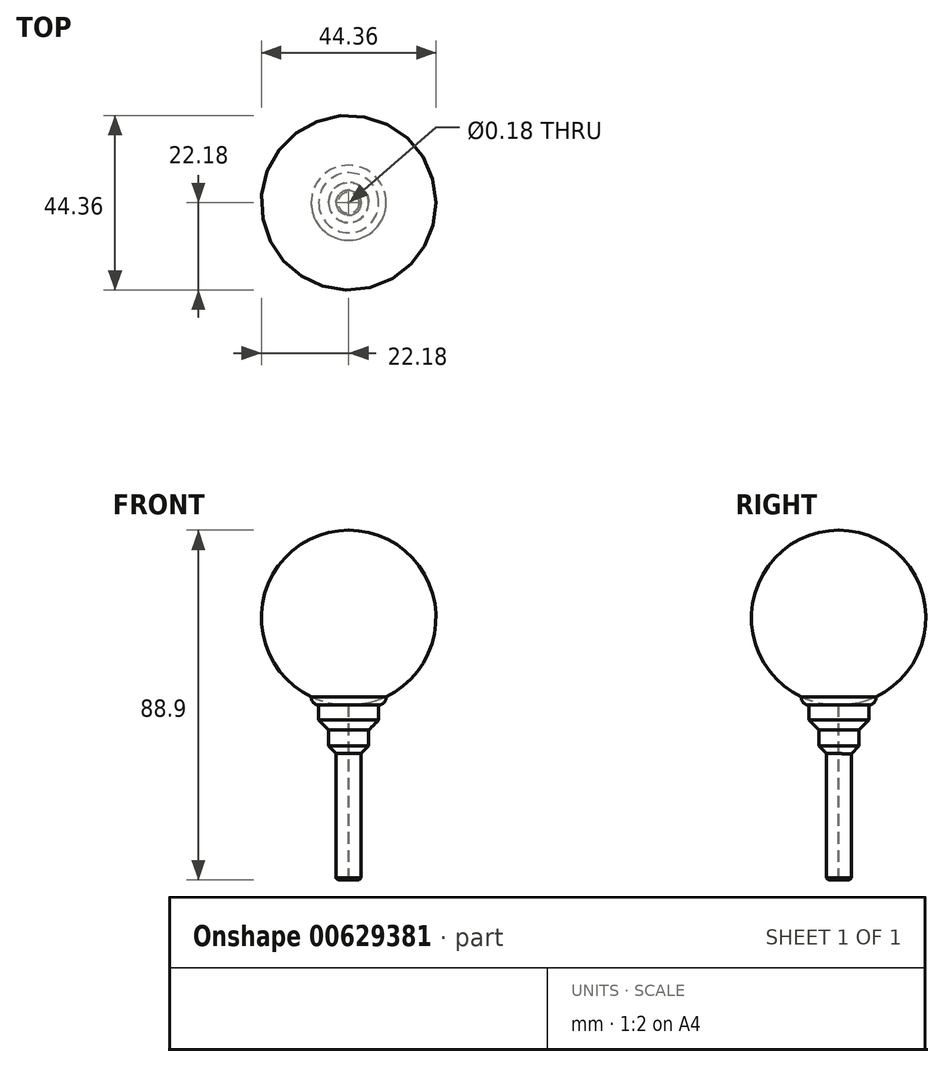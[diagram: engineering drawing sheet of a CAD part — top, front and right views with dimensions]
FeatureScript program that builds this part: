
annotation { "Feature Type Name" : "Feature", "Feature Type Description" : "" }
export const myFeature = defineFeature(function(context is Context, id is Id, definition is map)
    precondition{}
    {
        {
            var Q0;
            Q0=qCreatedBy(makeId("Front.planeOp"),FACE);
            var sketch = newSketch(context, id + "F0", { "sketchPlane" : qUnion([Q0])});
            skLineSegment(sketch, "E0", {"start": v(0, 0) * mm, "end": v(0, 44.45) * mm});
            skArc(sketch, "E1", {"start": v(0, 44.45) * mm, "mid": v(-22.27, 22.23) * mm, "end": v(0, 0) * mm});
            skSolve(sketch);
        }
        {
            var Q0;
            Q0=makeQuery(id+"F0.imprint","IMPRINT",FACE,{"disambiguationData":[TD([[makeQuery(id+"F0.imprint","IMPRINT",EDGE,{"derivedFrom":sQuery(id+"F0.wireOp",EDGE,"E0")}),1.0]])]});
            var Q1;
            Q1=sQuery(id+"F0.wireOp",EDGE,"E0");
            revolve(context, id + "F1", {"entities" : qUnion([Q0]), "axis" : qUnion([Q1]), "revolveType" : RevolveType.FULL});
        }
        {
            var Q0;
            Q0=qCreatedBy(makeId("Top.planeOp"),FACE);
            var sketch = newSketch(context, id + "F2", { "sketchPlane" : qUnion([Q0])});
            skCircle(sketch, "E2", {"center": v(0, 0) * mm, "radius": 9.53 * mm});
            skSolve(sketch);
        }
        {
            var Q0;
            Q0=makeQuery(id+"F2.imprint","IMPRINT",FACE,{"disambiguationData":[TD([[makeQuery(id+"F2.imprint","IMPRINT",EDGE,{"derivedFrom":sQuery(id+"F2.wireOp",EDGE,"E2")}),1.0]])]});
            extrude(context, id + "F3", {"entities" : qUnion([Q0]), "operationType" : NewBodyOperationType.ADD, "depth" : 19.05 * mm, "offsetDistance" : 25.4 * mm});
        }
        {
            var Q0;
            Q0=makeQuery(id+"F3.opExtrude","CAP_FACE",FACE,{"disambiguationData":[OSD([sQuery(id+"F2.wireOp",EDGE,"E2")])],"isStart":true});
            var sketch = newSketch(context, id + "F4", { "sketchPlane" : qUnion([Q0])});
            skCircle(sketch, "E3", {"center": v(0, 0) * mm, "radius": 7.62 * mm});
            skSolve(sketch);
        }
        {
            var Q0;
            Q0=makeQuery(id+"F4.imprint","IMPRINT",FACE,{"disambiguationData":[TD([[makeQuery(id+"F4.imprint","IMPRINT",EDGE,{"derivedFrom":sQuery(id+"F4.wireOp",EDGE,"E3")}),1.0]])]});
            extrude(context, id + "F5", {"entities" : qUnion([Q0]), "operationType" : NewBodyOperationType.ADD, "depth" : 6.35 * mm, "offsetDistance" : 25.4 * mm});
        }
        {
            var Q0;
            Q0=makeQuery(id+"F5.opExtrude","CAP_FACE",FACE,{"disambiguationData":[OSD([sQuery(id+"F0.wireOp",EDGE,"E1"),sQuery(id+"F2.wireOp",EDGE,"E2"),sQuery(id+"F4.wireOp",EDGE,"E3")])],"isStart":false});
            var sketch = newSketch(context, id + "F6", { "sketchPlane" : qUnion([Q0])});
            skCircle(sketch, "E4", {"center": v(0, -0.1) * mm, "radius": 5.08 * mm});
            skSolve(sketch);
        }
        {
            var Q0;
            Q0=makeQuery(id+"F6.imprint","IMPRINT",FACE,{"disambiguationData":[TD([[makeQuery(id+"F6.imprint","IMPRINT",EDGE,{"derivedFrom":sQuery(id+"F6.wireOp",EDGE,"E4")}),1.0]])]});
            extrude(context, id + "F7", {"entities" : qUnion([Q0]), "operationType" : NewBodyOperationType.ADD, "depth" : 6.35 * mm, "offsetDistance" : 25.4 * mm});
        }
        {
            var Q0;
            Q0=makeQuery(id+"F7.opExtrude","CAP_FACE",FACE,{"disambiguationData":[OSD([sQuery(id+"F0.wireOp",EDGE,"E1"),sQuery(id+"F2.wireOp",EDGE,"E2"),sQuery(id+"F6.wireOp",EDGE,"E4")])],"isStart":false});
            var sketch = newSketch(context, id + "F8", { "sketchPlane" : qUnion([Q0])});
            skCircle(sketch, "E5", {"center": v(0, 0) * mm, "radius": 3.18 * mm});
            skSolve(sketch);
        }
        {
            var Q0;
            Q0=makeQuery(id+"F8.imprint","IMPRINT",FACE,{"disambiguationData":[TD([[makeQuery(id+"F8.imprint","IMPRINT",EDGE,{"derivedFrom":sQuery(id+"F8.wireOp",EDGE,"E5")}),1.0]])]});
            extrude(context, id + "F9", {"entities" : qUnion([Q0]), "operationType" : NewBodyOperationType.ADD, "depth" : 31.75 * mm, "offsetDistance" : 25.4 * mm});
        }
        {
            var Q0;
            Q0=makeQuery(id+"F3.opExtrude","CAP_EDGE",EDGE,{"disambiguationData":[OSD([sQuery(id+"F2.wireOp",EDGE,"E2")])],"isStart":true});
            fillet(context, id + "F10", {"entities" : qUnion([Q0]), "radius" : 2.03 * mm, "tangentPropagation" : true, "allowEdgeOverflow" : false});
        }
        {
            var Q0;
            Q0=makeQuery(id+"F5.opExtrude","CAP_EDGE",EDGE,{"disambiguationData":[OSD([sQuery(id+"F4.wireOp",EDGE,"E3")])],"isStart":false});
            chamfer(context, id + "F11", {"entities" : qUnion([Q0]), "width" : 2.54 * mm, "tangentPropagation" : true});
        }
        {
            var Q0;
            Q0=makeQuery(id+"F7.opExtrude","CAP_EDGE",EDGE,{"disambiguationData":[OSD([sQuery(id+"F6.wireOp",EDGE,"E4")])],"isStart":false});
            chamfer(context, id + "F12", {"entities" : qUnion([Q0]), "width" : 2.3 * mm, "tangentPropagation" : true});
        }
        {
            var Q0;
            Q0=makeQuery(id+"F9.opExtrude","CAP_EDGE",EDGE,{"disambiguationData":[OSD([sQuery(id+"F8.wireOp",EDGE,"E5")])],"isStart":false});
            chamfer(context, id + "F13", {"entities" : qUnion([Q0]), "width" : 0.5 * mm, "tangentPropagation" : true});
        }
        {
            var Q0;
            Q0=qCreatedBy(makeId("Front.planeOp"),FACE);
            cPlane(context, id + "F14", {"entities" : qUnion([Q0]), "cplaneType" : CPlaneType.OFFSET, "offset" : 25.9 * mm, "oppositeDirection" : true, "width" : 152.4 * mm, "height" : 152.4 * mm});
        }
        {
            var Q0;
            Q0=qCreatedBy(id+"F14.planeOp",FACE);
            var sketch = newSketch(context, id + "F15", { "sketchPlane" : qUnion([Q0])});
            skCircle(sketch, "E6", {"center": v(0, 22.74) * mm, "radius": 15.88 * mm});
            skSolve(sketch);
        }
        {
            var Q0;
            Q0=makeQuery(id+"F15.imprint","IMPRINT",FACE,{"disambiguationData":[TD([[makeQuery(id+"F15.imprint","IMPRINT",EDGE,{"derivedFrom":sQuery(id+"F15.wireOp",EDGE,"E6")}),1.0]])]});
            extrude(context, id + "F16", {"entities" : qUnion([Q0]), "operationType" : NewBodyOperationType.ADD, "depth" : 17.78 * mm, "offsetDistance" : 25.4 * mm});
        }
        {
            var Q0;
            Q0=makeQuery(id+"F16.opExtrude","CAP_FACE",FACE,{"disambiguationData":[OSD([sQuery(id+"F15.wireOp",EDGE,"E6")])],"isStart":true});
            var sketch = newSketch(context, id + "F17", { "sketchPlane" : qUnion([Q0])});
            skCircle(sketch, "E7", {"center": v(0, 22.74) * mm, "radius": 12.7 * mm});
            skSolve(sketch);
        }
        {
            var Q0;
            Q0=makeQuery(id+"F17.imprint","IMPRINT",FACE,{"disambiguationData":[TD([[makeQuery(id+"F17.imprint","IMPRINT",EDGE,{"derivedFrom":sQuery(id+"F17.wireOp",EDGE,"E7")}),1.0]])]});
            extrude(context, id + "F18", {"entities" : qUnion([Q0]), "operationType" : NewBodyOperationType.ADD, "depth" : 19.05 * mm, "offsetDistance" : 25.4 * mm});
        }
        {
            var Q0;
            Q0=makeQuery(id+"F18.opExtrude","CAP_FACE",FACE,{"disambiguationData":[OSD([sQuery(id+"F17.wireOp",EDGE,"E7")])],"isStart":false});
            var sketch = newSketch(context, id + "F19", { "sketchPlane" : qUnion([Q0])});
            skCircle(sketch, "E8", {"center": v(0, 22.74) * mm, "radius": 9.53 * mm});
            skSolve(sketch);
        }
        {
            var Q0;
            Q0=makeQuery(id+"F19.imprint","IMPRINT",FACE,{"disambiguationData":[TD([[makeQuery(id+"F19.imprint","IMPRINT",EDGE,{"derivedFrom":sQuery(id+"F19.wireOp",EDGE,"E8")}),1.0]])]});
            extrude(context, id + "F20", {"entities" : qUnion([Q0]), "operationType" : NewBodyOperationType.ADD, "depth" : 17.78 * mm, "offsetDistance" : 25.4 * mm});
        }
        {
            var Q0;
            Q0=makeQuery(id+"F20.opExtrude","CAP_FACE",FACE,{"disambiguationData":[OSD([sQuery(id+"F19.wireOp",EDGE,"E8")])],"isStart":false});
            var sketch = newSketch(context, id + "F21", { "sketchPlane" : qUnion([Q0])});
            skCircle(sketch, "E9", {"center": v(0, 22.74) * mm, "radius": 6.35 * mm});
            skSolve(sketch);
        }
        {
            var Q0;
            Q0=makeQuery(id+"F21.imprint","IMPRINT",FACE,{"disambiguationData":[TD([[makeQuery(id+"F21.imprint","IMPRINT",EDGE,{"derivedFrom":sQuery(id+"F21.wireOp",EDGE,"E9")}),1.0]])]});
            extrude(context, id + "F22", {"entities" : qUnion([Q0]), "operationType" : NewBodyOperationType.ADD, "depth" : 68.58 * mm, "offsetDistance" : 25.4 * mm});
        }
        {
            var Q0;
            Q0=makeQuery(id+"F16.opExtrude","CAP_EDGE",EDGE,{"disambiguationData":[OSD([sQuery(id+"F15.wireOp",EDGE,"E6")])],"isStart":true});
            fillet(context, id + "F23", {"entities" : qUnion([Q0]), "radius" : 15.87 * mm, "tangentPropagation" : true, "allowEdgeOverflow" : false});
        }
        {
            var Q0;
            Q0=makeQuery(id+"F18.opExtrude","CAP_EDGE",EDGE,{"disambiguationData":[OSD([sQuery(id+"F17.wireOp",EDGE,"E7")])],"isStart":false});
            chamfer(context, id + "F24", {"entities" : qUnion([Q0]), "width" : 6.35 * mm, "tangentPropagation" : true});
        }
        {
            var Q0;
            Q0=makeQuery(id+"F20.opExtrude","CAP_EDGE",EDGE,{"disambiguationData":[OSD([sQuery(id+"F19.wireOp",EDGE,"E8")])],"isStart":false});
            chamfer(context, id + "F25", {"entities" : qUnion([Q0]), "width" : 7.62 * mm, "tangentPropagation" : true});
        }
        {
            var Q0;
            Q0=makeQuery(id+"F22.opExtrude","CAP_EDGE",EDGE,{"disambiguationData":[OSD([sQuery(id+"F21.wireOp",EDGE,"E9")])],"isStart":false});
            chamfer(context, id + "F26", {"entities" : qUnion([Q0]), "width" : 1.02 * mm, "tangentPropagation" : true});
        }
        {
            var Q0;
            Q0=qCreatedBy(makeId("Right.planeOp"),FACE);
            cPlane(context, id + "F27", {"entities" : qUnion([Q0]), "cplaneType" : CPlaneType.OFFSET, "offset" : 24.64 * mm, "width" : 152.4 * mm, "height" : 152.4 * mm});
        }
        {
            var Q0;
            Q0=qCreatedBy(id+"F27.planeOp",FACE);
            var sketch = newSketch(context, id + "F28", { "sketchPlane" : qUnion([Q0])});
            skCircle(sketch, "E10", {"center": v(0, 22.78) * mm, "radius": 7.62 * mm});
            skSolve(sketch);
        }
        {
            var Q0;
            Q0=makeQuery(id+"F28.imprint","IMPRINT",FACE,{"disambiguationData":[TD([[makeQuery(id+"F28.imprint","IMPRINT",EDGE,{"derivedFrom":sQuery(id+"F28.wireOp",EDGE,"E10")}),1.0]])]});
            extrude(context, id + "F29", {"entities" : qUnion([Q0]), "operationType" : NewBodyOperationType.ADD, "oppositeDirection" : true, "depth" : 15.24 * mm, "offsetDistance" : 25.4 * mm});
        }
        {
            var Q0;
            Q0=makeQuery(id+"F29.opExtrude","CAP_FACE",FACE,{"disambiguationData":[OSD([sQuery(id+"F28.wireOp",EDGE,"E10")])],"isStart":true});
            var sketch = newSketch(context, id + "F30", { "sketchPlane" : qUnion([Q0])});
            skCircle(sketch, "E11", {"center": v(0, 22.78) * mm, "radius": 4.45 * mm});
            skSolve(sketch);
        }
        {
            var Q0;
            Q0=makeQuery(id+"F30.imprint","IMPRINT",FACE,{"disambiguationData":[TD([[makeQuery(id+"F30.imprint","IMPRINT",EDGE,{"derivedFrom":sQuery(id+"F30.wireOp",EDGE,"E11")}),1.0]])]});
            extrude(context, id + "F31", {"entities" : qUnion([Q0]), "operationType" : NewBodyOperationType.ADD, "depth" : 3.8 * mm, "offsetDistance" : 25.4 * mm});
        }
        {
            var Q0;
            Q0=makeQuery(id+"F31.opExtrude","CAP_FACE",FACE,{"disambiguationData":[OSD([sQuery(id+"F30.wireOp",EDGE,"E11")])],"isStart":false});
            var sketch = newSketch(context, id + "F32", { "sketchPlane" : qUnion([Q0])});
            skCircle(sketch, "E12", {"center": v(0, 22.78) * mm, "radius": 2.54 * mm});
            skSolve(sketch);
        }
        {
            var Q0;
            Q0=makeQuery(id+"F32.imprint","IMPRINT",FACE,{"disambiguationData":[TD([[makeQuery(id+"F32.imprint","IMPRINT",EDGE,{"derivedFrom":sQuery(id+"F32.wireOp",EDGE,"E12")}),1.0]])]});
            extrude(context, id + "F33", {"entities" : qUnion([Q0]), "operationType" : NewBodyOperationType.ADD, "depth" : 4.06 * mm, "offsetDistance" : 25.4 * mm});
        }
        {
            var Q0;
            Q0=makeQuery(id+"F33.opExtrude","CAP_FACE",FACE,{"disambiguationData":[OSD([sQuery(id+"F32.wireOp",EDGE,"E12")])],"isStart":false});
            var sketch = newSketch(context, id + "F34", { "sketchPlane" : qUnion([Q0])});
            skCircle(sketch, "E13", {"center": v(0, 22.78) * mm, "radius": 1.59 * mm});
            skSolve(sketch);
        }
        {
            var Q0;
            Q0=makeQuery(id+"F34.imprint","IMPRINT",FACE,{"disambiguationData":[TD([[makeQuery(id+"F34.imprint","IMPRINT",EDGE,{"derivedFrom":sQuery(id+"F34.wireOp",EDGE,"E13")}),1.0]])]});
            extrude(context, id + "F35", {"entities" : qUnion([Q0]), "operationType" : NewBodyOperationType.ADD, "depth" : 25.4 * mm, "offsetDistance" : 25.4 * mm});
        }
        {
            var Q0;
            Q0=makeQuery(id+"F29.opExtrude","CAP_EDGE",EDGE,{"disambiguationData":[OSD([sQuery(id+"F28.wireOp",EDGE,"E10")])],"isStart":true});
            fillet(context, id + "F36", {"entities" : qUnion([Q0]), "radius" : 3.8 * mm, "tangentPropagation" : true, "allowEdgeOverflow" : false});
        }
        {
            var Q0;
            Q0=makeQuery(id+"F31.opExtrude","CAP_EDGE",EDGE,{"disambiguationData":[OSD([sQuery(id+"F30.wireOp",EDGE,"E11")])],"isStart":false});
            chamfer(context, id + "F37", {"entities" : qUnion([Q0]), "width" : 1.52 * mm, "tangentPropagation" : true});
        }
        {
            var Q0;
            Q0=makeQuery(id+"F33.opExtrude","CAP_EDGE",EDGE,{"disambiguationData":[OSD([sQuery(id+"F32.wireOp",EDGE,"E12")])],"isStart":false});
            chamfer(context, id + "F38", {"entities" : qUnion([Q0]), "width" : 1.27 * mm, "tangentPropagation" : true});
        }
        {
            var Q0;
            Q0=makeQuery(id+"F35.opExtrude","CAP_EDGE",EDGE,{"disambiguationData":[OSD([sQuery(id+"F34.wireOp",EDGE,"E13")])],"isStart":false});
            chamfer(context, id + "F39", {"entities" : qUnion([Q0]), "width" : 0.28 * mm, "tangentPropagation" : true});
        }
    });
